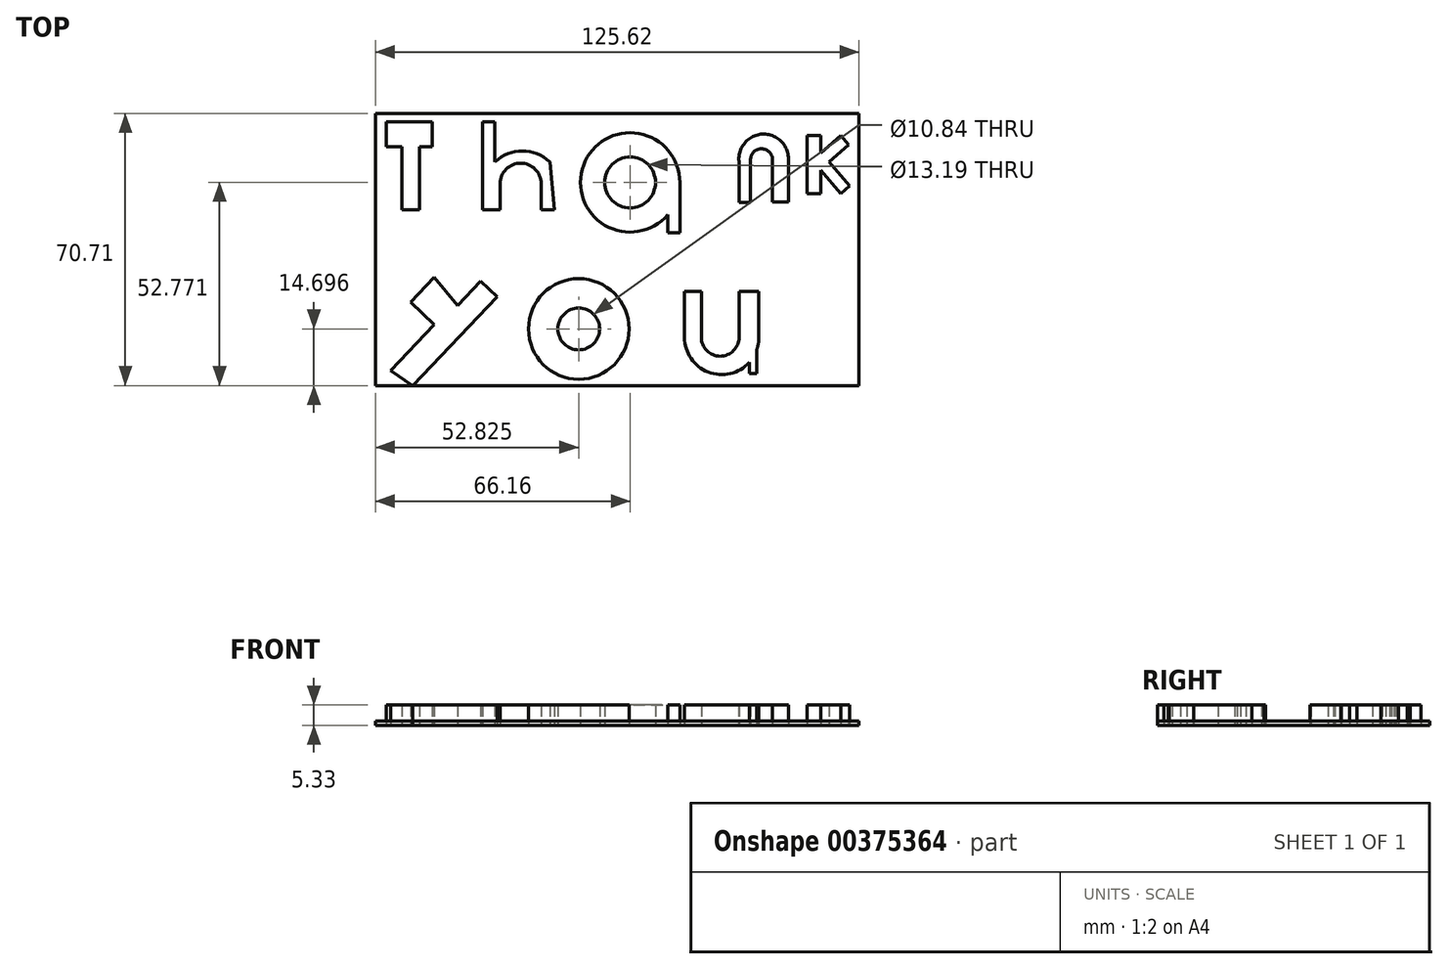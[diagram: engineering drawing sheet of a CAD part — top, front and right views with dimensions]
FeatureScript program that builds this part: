
annotation { "Feature Type Name" : "Feature", "Feature Type Description" : "" }
export const myFeature = defineFeature(function(context is Context, id is Id, definition is map)
    precondition{}
    {
        {
            var Q0;
            Q0=qCreatedBy(makeId("Top.planeOp"),FACE);
            var sketch = newSketch(context, id + "F0", { "sketchPlane" : qUnion([Q0])});
            skLineSegment(sketch, "E0", {"start": v(-63.4, 68.49) * mm, "end": v(-51.44, 68.49) * mm});
            skLineSegment(sketch, "E1", {"start": v(-51.44, 68.49) * mm, "end": v(-51.44, 62.05) * mm});
            skLineSegment(sketch, "E2", {"start": v(-51.44, 62.05) * mm, "end": v(-54.7, 62.05) * mm});
            skLineSegment(sketch, "E3", {"start": v(-54.7, 62.05) * mm, "end": v(-54.7, 45.72) * mm});
            skLineSegment(sketch, "E4", {"start": v(-54.7, 45.72) * mm, "end": v(-59.33, 45.72) * mm});
            skLineSegment(sketch, "E5", {"start": v(-59.33, 45.72) * mm, "end": v(-59.33, 62.05) * mm});
            skLineSegment(sketch, "E6", {"start": v(-59.33, 62.05) * mm, "end": v(-63.4, 62.05) * mm});
            skLineSegment(sketch, "E7", {"start": v(-63.4, 62.05) * mm, "end": v(-63.4, 68.49) * mm});
            skLineSegment(sketch, "E8", {"start": v(-38.37, 68.49) * mm, "end": v(-38.37, 45.72) * mm});
            skLineSegment(sketch, "E9", {"start": v(-38.37, 45.72) * mm, "end": v(-33.75, 45.72) * mm});
            skLineSegment(sketch, "E10", {"start": v(-38.37, 68.49) * mm, "end": v(-35.1, 68.49) * mm});
            skLineSegment(sketch, "E11", {"start": v(-23.13, 45.72) * mm, "end": v(-19.62, 45.72) * mm});
            skLineSegment(sketch, "E12", {"start": v(28.3, 58.24) * mm, "end": v(28.3, 47.63) * mm});
            skLineSegment(sketch, "E13", {"start": v(28.3, 47.63) * mm, "end": v(31.3, 47.63) * mm});
            skLineSegment(sketch, "E14", {"start": v(31.3, 47.63) * mm, "end": v(31.3, 58.51) * mm});
            skLineSegment(sketch, "E15.MirrorCS", {"start": v(37.03, 47.75) * mm, "end": v(37.03, 58.64) * mm});
            skLineSegment(sketch, "E16", {"start": v(37.03, 47.75) * mm, "end": v(41.16, 47.75) * mm});
            skLineSegment(sketch, "E17", {"start": v(41.16, 47.75) * mm, "end": v(41.16, 58.88) * mm});
            skArc(sketch, "E18", {"start": v(37.03, 58.64) * mm, "mid": v(34.1, 61.5) * mm, "end": v(31.3, 58.51) * mm});
            skArc(sketch, "E19", {"start": v(41.16, 58.88) * mm, "mid": v(34.39, 65.32) * mm, "end": v(28.3, 58.24) * mm});
            skLineSegment(sketch, "E20", {"start": v(46.04, 64.15) * mm, "end": v(46.04, 49.9) * mm});
            skLineSegment(sketch, "E21", {"start": v(46.04, 49.9) * mm, "end": v(49.5, 49.9) * mm});
            skLineSegment(sketch, "E22", {"start": v(49.5, 49.9) * mm, "end": v(49.5, 55.93) * mm});
            skLineSegment(sketch, "E23", {"start": v(49.5, 55.93) * mm, "end": v(54.77, 49.9) * mm});
            skLineSegment(sketch, "E24", {"start": v(54.77, 49.9) * mm, "end": v(57.05, 51.88) * mm});
            skLineSegment(sketch, "E25", {"start": v(57.05, 51.88) * mm, "end": v(51.65, 58.07) * mm});
            skLineSegment(sketch, "E26", {"start": v(51.65, 58.07) * mm, "end": v(56.84, 62.6) * mm});
            skLineSegment(sketch, "E27", {"start": v(56.84, 62.6) * mm, "end": v(54.77, 64.96) * mm});
            skLineSegment(sketch, "E28", {"start": v(54.77, 64.96) * mm, "end": v(49.5, 60.37) * mm});
            skLineSegment(sketch, "E29", {"start": v(49.5, 60.37) * mm, "end": v(49.5, 64.96) * mm});
            skLineSegment(sketch, "E30", {"start": v(49.5, 64.96) * mm, "end": v(46.04, 64.96) * mm});
            skLineSegment(sketch, "E31", {"start": v(46.04, 64.96) * mm, "end": v(46.04, 64.15) * mm});
            skCircle(sketch, "E32", {"center": v(-13.34, 14.7) * mm, "radius": 13.07 * mm});
            skCircle(sketch, "E33", {"center": v(-13.34, 14.7) * mm, "radius": 5.42 * mm});
            skLineSegment(sketch, "E34", {"start": v(18.5, 24.48) * mm, "end": v(18.5, 12.52) * mm});
            skLineSegment(sketch, "E35", {"start": v(28.3, 24.5) * mm, "end": v(28.3, 12.52) * mm});
            skLineSegment(sketch, "E36", {"start": v(28.3, 24.5) * mm, "end": v(33.46, 24.5) * mm});
            skLineSegment(sketch, "E37", {"start": v(33.46, 24.5) * mm, "end": v(33.46, 12.51) * mm});
            skLineSegment(sketch, "E38", {"start": v(18.5, 24.48) * mm, "end": v(14.14, 24.48) * mm});
            skLineSegment(sketch, "E39", {"start": v(14.14, 24.48) * mm, "end": v(14.14, 12.51) * mm});
            skArc(sketch, "E40", {"start": v(18.5, 12.52) * mm, "mid": v(23.4, 7.62) * mm, "end": v(28.3, 12.52) * mm});
            skArc(sketch, "E41", {"start": v(14.14, 12.51) * mm, "mid": v(20.32, 3.5) * mm, "end": v(30.95, 6.02) * mm});
            skLineSegment(sketch, "E42", {"start": v(32.95, 9.4) * mm, "end": v(32.95, 3.14) * mm});
            skLineSegment(sketch, "E43", {"start": v(32.95, 3.14) * mm, "end": v(31.05, 3.08) * mm});
            skLineSegment(sketch, "E44", {"start": v(31.05, 3.08) * mm, "end": v(30.95, 6.02) * mm});
            skArc(sketch, "E45.trimOffspring", {"start": v(32.95, 9.4) * mm, "mid": v(33.33, 10.94) * mm, "end": v(33.46, 12.51) * mm});
            skLineSegment(sketch, "E46", {"start": v(-56.47, 0) * mm, "end": v(-34.59, 23.06) * mm});
            skLineSegment(sketch, "E47", {"start": v(-34.59, 23.06) * mm, "end": v(-38.82, 27.07) * mm});
            skLineSegment(sketch, "E48", {"start": v(-38.82, 27.07) * mm, "end": v(-44.86, 20.7) * mm});
            skLineSegment(sketch, "E49", {"start": v(-62.22, 3.84) * mm, "end": v(-56.47, 0) * mm});
            skLineSegment(sketch, "E50", {"start": v(-62.22, 3.84) * mm, "end": v(-50.9, 15.78) * mm});
            skLineSegment(sketch, "E51", {"start": v(-50.9, 15.78) * mm, "end": v(-57.05, 21.63) * mm});
            skLineSegment(sketch, "E52", {"start": v(-57.05, 21.63) * mm, "end": v(-50.9, 28.13) * mm});
            skLineSegment(sketch, "E53", {"start": v(-50.9, 28.13) * mm, "end": v(-44.86, 20.7) * mm});
            skLineSegment(sketch, "E54", {"start": v(-33.75, 45.72) * mm, "end": v(-33.75, 52.48) * mm});
            skLineSegment(sketch, "E55", {"start": v(-23.13, 45.72) * mm, "end": v(-23.13, 52.48) * mm});
            skArc(sketch, "E56", {"start": v(-23.13, 52.48) * mm, "mid": v(-28.44, 57.79) * mm, "end": v(-33.75, 52.48) * mm});
            skPoint(sketch, "E57.end.orphan", {"position": v(-35.1, 62.05) * mm});
            skLineSegment(sketch, "E58", {"start": v(-35.1, 68.49) * mm, "end": v(-35.1, 58.1) * mm});
            skArc(sketch, "E59", {"start": v(-20.87, 58.1) * mm, "mid": v(-27.99, 60.93) * mm, "end": v(-35.1, 58.1) * mm});
            skLineSegment(sketch, "E60", {"start": v(-19.62, 45.72) * mm, "end": v(-20.87, 58.1) * mm});
            skPoint(sketch, "E61.center.orphan", {"position": v(0, 60.53) * mm});
            skCircle(sketch, "E62", {"center": v(0, 52.77) * mm, "radius": 12.9 * mm});
            skCircle(sketch, "E63", {"center": v(0, 52.77) * mm, "radius": 6.6 * mm});
            skLineSegment(sketch, "E64", {"start": v(9.78, 44.35) * mm, "end": v(9.78, 39.7) * mm});
            skLineSegment(sketch, "E65", {"start": v(9.78, 39.7) * mm, "end": v(12.9, 39.7) * mm});
            skLineSegment(sketch, "E66", {"start": v(12.9, 39.7) * mm, "end": v(12.9, 52.77) * mm});
            skSolve(sketch);
        }
        {
            var Q0;
            Q0=makeQuery(id+"F0.imprint","IMPRINT",FACE,{"disambiguationData":[TD([[makeQuery(id+"F0.imprint","IMPRINT",EDGE,{"derivedFrom":sQuery(id+"F0.wireOp",EDGE,"E0")}),-1.0]])]});
            var Q1;
            Q1=makeQuery(id+"F0.imprint","IMPRINT",FACE,{"disambiguationData":[TD([[makeQuery(id+"F0.imprint","IMPRINT",EDGE,{"derivedFrom":sQuery(id+"F0.wireOp",EDGE,"E8")}),1.0]])]});
            var Q2;
            Q2=makeQuery(id+"F0.imprint","IMPRINT",FACE,{"disambiguationData":[TD([[makeQuery(id+"F0.imprint","IMPRINT",EDGE,{"derivedFrom":sQuery(id+"F0.wireOp",EDGE,"E12")}),1.0]])]});
            var Q3;
            Q3=makeQuery(id+"F0.imprint","IMPRINT",FACE,{"disambiguationData":[TD([[makeQuery(id+"F0.imprint","IMPRINT",EDGE,{"derivedFrom":sQuery(id+"F0.wireOp",EDGE,"E20")}),1.0]])]});
            var Q4;
            Q4=makeQuery(id+"F0.imprint","IMPRINT",FACE,{"disambiguationData":[TD([[makeQuery(id+"F0.imprint","IMPRINT",EDGE,{"derivedFrom":sQuery(id+"F0.wireOp",EDGE,"E34")}),-1.0]])]});
            var Q5;
            Q5=makeQuery(id+"F0.imprint","IMPRINT",FACE,{"disambiguationData":[TD([[makeQuery(id+"F0.imprint","IMPRINT",EDGE,{"derivedFrom":sQuery(id+"F0.wireOp",EDGE,"E46")}),1.0]])]});
            var Q6;
            Q6=makeQuery(id+"F0.imprint","IMPRINT",FACE,{"disambiguationData":[TD([[makeQuery(id+"F0.imprint","IMPRINT",EDGE,{"derivedFrom":sQuery(id+"F0.wireOp",EDGE,"E32")}),1.0]])]});
            var Q7;
            Q7=makeQuery(id+"F0.imprint","IMPRINT",FACE,{"disambiguationData":[TD([[makeQuery(id+"F0.imprint","IMPRINT",EDGE,{"derivedFrom":sQuery(id+"F0.wireOp",EDGE,"E62")}),1.0]])]});
            var Q8;
            {var subQ0=sQuery(id+"F0.wireOp",EDGE,"E64");Q8=makeQuery(id+"F0.imprint","IMPRINT",FACE,{"disambiguationData":[TD([[makeQuery(id+"F0.imprint","IMPRINT",EDGE,{"derivedFrom":subQ0}),1.0]])]});}
            extrude(context, id + "F1", {"entities" : qUnion([Q0, Q1, Q2, Q3, Q4, Q5, Q6, Q7, Q8]), "depth" : 5.33 * mm});
        }
        {
            var Q0;
            Q0=qCreatedBy(makeId("Top.planeOp"),FACE);
            var sketch = newSketch(context, id + "F2", { "sketchPlane" : qUnion([Q0])});
            skLineSegment(sketch, "E67.bottom", {"start": v(-66.16, 70.71) * mm, "end": v(59.46, 70.71) * mm});
            skLineSegment(sketch, "E67.top", {"start": v(-66.16, 0) * mm, "end": v(59.46, 0) * mm});
            skLineSegment(sketch, "E67.left", {"start": v(-66.16, 70.71) * mm, "end": v(-66.16, 0) * mm});
            skLineSegment(sketch, "E67.right", {"start": v(59.46, 70.71) * mm, "end": v(59.46, 0) * mm});
            skSolve(sketch);
        }
        {
            var Q0;
            Q0=makeQuery(id+"F2.imprint","IMPRINT",FACE,{"disambiguationData":[TD([[makeQuery(id+"F2.imprint","IMPRINT",EDGE,{"derivedFrom":sQuery(id+"F2.wireOp",EDGE,"E67.bottom")}),-1.0]])]});
            extrude(context, id + "F3", {"entities" : qUnion([Q0]), "depth" : 1.2 * mm});
        }
    });
